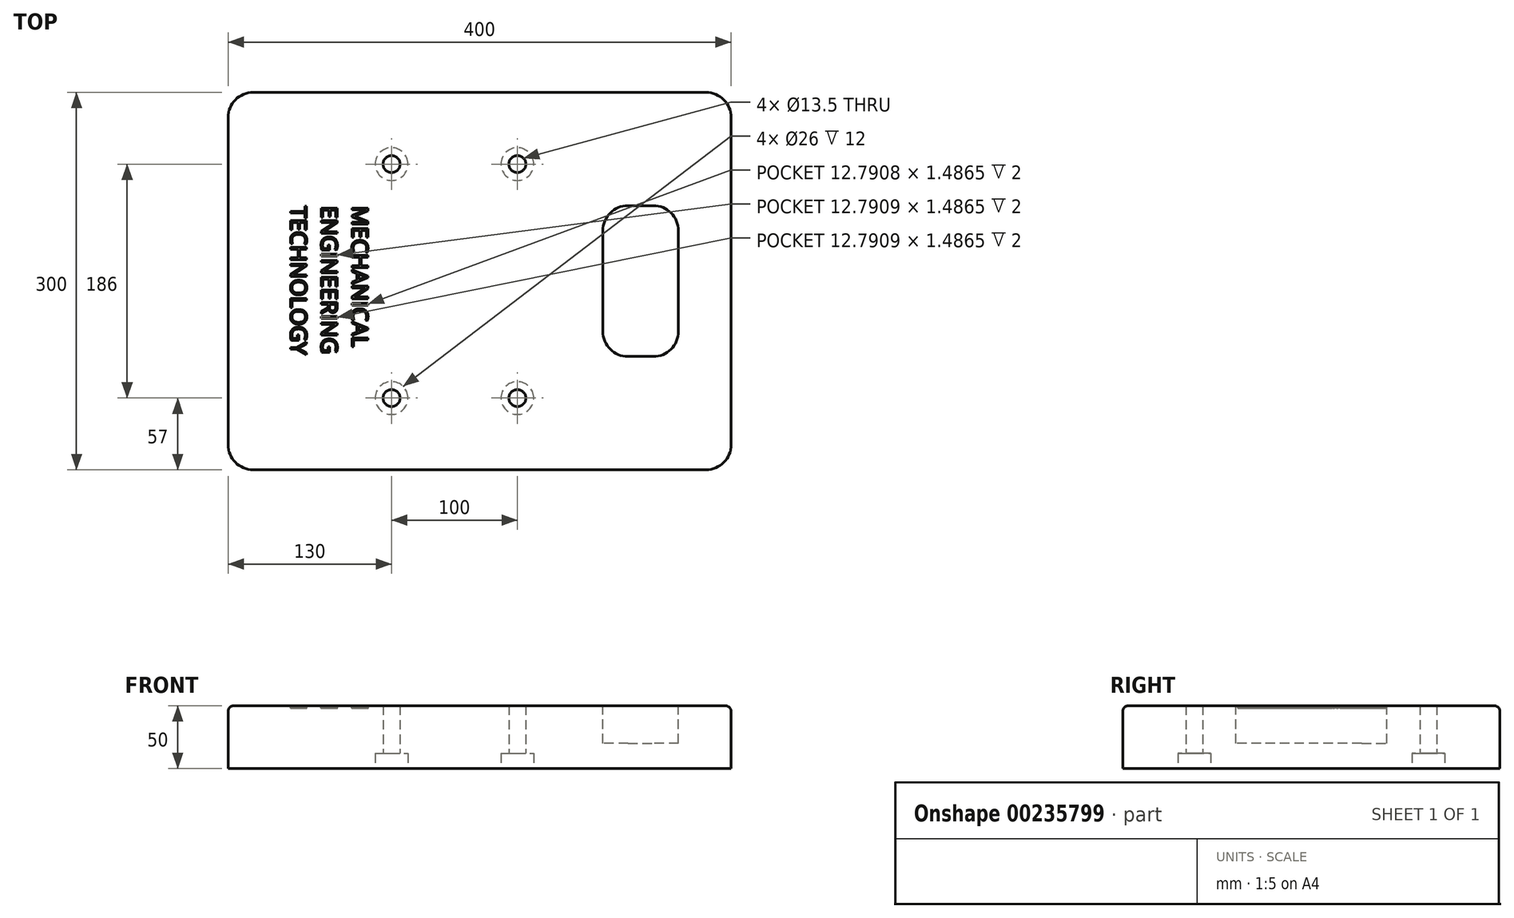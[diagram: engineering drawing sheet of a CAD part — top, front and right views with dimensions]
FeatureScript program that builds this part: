
annotation { "Feature Type Name" : "Feature", "Feature Type Description" : "" }
export const myFeature = defineFeature(function(context is Context, id is Id, definition is map)
    precondition{}
    {
        {
            var Q0;
            Q0=qCreatedBy(makeId("Top.planeOp"),FACE);
            var sketch = newSketch(context, id + "F0", { "sketchPlane" : qUnion([Q0])});
            skLineSegment(sketch, "E0", {"start": v(0, 0) * mm, "end": v(-200, 0) * mm});
            skLineSegment(sketch, "E1", {"start": v(-200, 0) * mm, "end": v(200, 0) * mm});
            skLineSegment(sketch, "E2", {"start": v(200, 0) * mm, "end": v(200, 150) * mm});
            skLineSegment(sketch, "E3", {"start": v(200, 150) * mm, "end": v(200, -150) * mm});
            skLineSegment(sketch, "E4", {"start": v(200, -150) * mm, "end": v(-200, -150) * mm});
            skLineSegment(sketch, "E5", {"start": v(-200, -150) * mm, "end": v(-200, 0) * mm});
            skLineSegment(sketch, "E6", {"start": v(-200, 0) * mm, "end": v(-200, 150) * mm});
            skLineSegment(sketch, "E7", {"start": v(-200, 150) * mm, "end": v(200, 150) * mm});
            skSolve(sketch);
        }
        {
            var Q0;
            {var subQ0=sQuery(id+"F0.wireOp",EDGE,"E4");Q0=makeQuery(id+"F0.imprint","IMPRINT",FACE,{"disambiguationData":[TD([[makeQuery(id+"F0.imprint","IMPRINT",EDGE,{"derivedFrom":subQ0}),-1.0]])]});}
            var Q1;
            {var subQ4=sQuery(id+"F0.wireOp",EDGE,"E6");Q1=makeQuery(id+"F0.imprint","IMPRINT",FACE,{"disambiguationData":[TD([[makeQuery(id+"F0.imprint","IMPRINT",EDGE,{"derivedFrom":subQ4}),-1.0]])]});}
            extrude(context, id + "F1", {"entities" : qUnion([Q0, Q1]), "depth" : 50 * mm});
        }
        {
            var Q0;
            Q0=makeQuery(id+"F1.opExtrude","SWEPT_EDGE",EDGE,{"disambiguationData":[OSD([sQuery(id+"F0.wireOp",EDGE,"E3"),sQuery(id+"F0.wireOp",EDGE,"E4")])]});
            var Q1;
            Q1=makeQuery(id+"F1.opExtrude","SWEPT_EDGE",EDGE,{"disambiguationData":[OSD([sQuery(id+"F0.wireOp",EDGE,"E3"),sQuery(id+"F0.wireOp",EDGE,"E7")])]});
            var Q2;
            Q2=makeQuery(id+"F1.opExtrude","SWEPT_EDGE",EDGE,{"disambiguationData":[OSD([sQuery(id+"F0.wireOp",EDGE,"E6"),sQuery(id+"F0.wireOp",EDGE,"E7")])]});
            var Q3;
            Q3=makeQuery(id+"F1.opExtrude","SWEPT_EDGE",EDGE,{"disambiguationData":[OSD([sQuery(id+"F0.wireOp",EDGE,"E4"),sQuery(id+"F0.wireOp",EDGE,"E5")])]});
            fillet(context, id + "F2", {"entities" : qUnion([Q0, Q1, Q2, Q3]), "radius" : 20 * mm, "tangentPropagation" : true, "allowEdgeOverflow" : false});
        }
        {
            var Q0;
            Q0=makeQuery(id+"F1.opExtrude","CAP_FACE",FACE,{"disambiguationData":[OSD([sQuery(id+"F0.wireOp",EDGE,"E3"),sQuery(id+"F0.wireOp",EDGE,"E4"),sQuery(id+"F0.wireOp",EDGE,"E5"),sQuery(id+"F0.wireOp",EDGE,"E6"),sQuery(id+"F0.wireOp",EDGE,"E7")])],"isStart":false});
            var sketch = newSketch(context, id + "F3", { "sketchPlane" : qUnion([Q0])});
            skLineSegment(sketch, "E8", {"start": v(-200, 0) * mm, "end": v(98, 0) * mm});
            skPoint(sketch, "E8.endSnap0", {"position": v(-200, 0) * mm});
            skLineSegment(sketch, "E9", {"start": v(98, 0) * mm, "end": v(98, 40) * mm});
            skLineSegment(sketch, "E10", {"start": v(118, 60) * mm, "end": v(138, 60) * mm});
            skLineSegment(sketch, "E11", {"start": v(158, 40) * mm, "end": v(158, -40) * mm});
            skLineSegment(sketch, "E12", {"start": v(138, -60) * mm, "end": v(118, -60) * mm});
            skLineSegment(sketch, "E13", {"start": v(98, -40) * mm, "end": v(98, 0) * mm});
            skPoint(sketch, "E14.visualSharp", {"position": v(158, -60) * mm});
            skArc(sketch, "E14.filletArc", {"start": v(138, -60) * mm, "mid": v(152.14, -54.14) * mm, "end": v(158, -40) * mm});
            skPoint(sketch, "E15.visualSharp", {"position": v(158, 60) * mm});
            skArc(sketch, "E15.filletArc", {"start": v(158, 40) * mm, "mid": v(152.14, 54.14) * mm, "end": v(138, 60) * mm});
            skPoint(sketch, "E16.visualSharp", {"position": v(98, 60) * mm});
            skArc(sketch, "E16.filletArc", {"start": v(118, 60) * mm, "mid": v(103.86, 54.14) * mm, "end": v(98, 40) * mm});
            skPoint(sketch, "E17.visualSharp", {"position": v(98, -60) * mm});
            skArc(sketch, "E17.filletArc", {"start": v(98, -40) * mm, "mid": v(103.86, -54.14) * mm, "end": v(118, -60) * mm});
            skSolve(sketch);
        }
        {
            var Q0;
            Q0=makeQuery(id+"F3.imprint","IMPRINT",FACE,{"disambiguationData":[TD([[makeQuery(id+"F3.imprint","IMPRINT",EDGE,{"derivedFrom":sQuery(id+"F3.wireOp",EDGE,"E9")}),-1.0]])]});
            extrude(context, id + "F4", {"entities" : qUnion([Q0]), "operationType" : NewBodyOperationType.REMOVE, "oppositeDirection" : true, "depth" : 30 * mm});
        }
        {
            var Q0;
            Q0=makeQuery(id+"F1.opExtrude","CAP_FACE",FACE,{"disambiguationData":[OSD([sQuery(id+"F0.wireOp",EDGE,"E3"),sQuery(id+"F0.wireOp",EDGE,"E4"),sQuery(id+"F0.wireOp",EDGE,"E5"),sQuery(id+"F0.wireOp",EDGE,"E6"),sQuery(id+"F0.wireOp",EDGE,"E7")])],"isStart":true});
            var sketch = newSketch(context, id + "F5", { "sketchPlane" : qUnion([Q0])});
            skLineSegment(sketch, "E18", {"start": v(200, -93) * mm, "end": v(30, -93) * mm});
            skLineSegment(sketch, "E19", {"start": v(30, -93) * mm, "end": v(30, 93) * mm});
            skLineSegment(sketch, "E20", {"start": v(30, 93) * mm, "end": v(-70, 93) * mm});
            skLineSegment(sketch, "E21", {"start": v(-70, 93) * mm, "end": v(-70, -93) * mm});
            skLineSegment(sketch, "E22", {"start": v(-70, -93) * mm, "end": v(30, -93) * mm});
            skCircle(sketch, "E23", {"center": v(30, 93) * mm, "radius": 6.75 * mm});
            skLineSegment(sketch, "E24", {"start": v(-20, -93) * mm, "end": v(-20, 93) * mm});
            skLineSegment(sketch, "E25", {"start": v(-70, 0) * mm, "end": v(30, 0) * mm});
            skCircle(sketch, "E26.MirrorC", {"center": v(-70, 93) * mm, "radius": 6.75 * mm});
            skCircle(sketch, "E27.MirrorC", {"center": v(-70, -93) * mm, "radius": 6.75 * mm});
            skCircle(sketch, "E28.MirrorC", {"center": v(30, -93) * mm, "radius": 6.75 * mm});
            skLineSegment(sketch, "E29", {"start": v(200, 0) * mm, "end": v(36.1, 0) * mm});
            skLineSegment(sketch, "E30", {"start": v(174.34, -93) * mm, "end": v(174.34, 0) * mm});
            skPoint(sketch, "E30.endSnap0", {"position": v(118.05, 0) * mm});
            skSolve(sketch);
        }
        {
            var Q0;
            Q0=sQuery(id+"F5.wireOp",VERTEX,"E21.start");
            var Q1;
            Q1=sQuery(id+"F5.wireOp",VERTEX,"E20.start");
            var Q2;
            Q2=sQuery(id+"F5.wireOp",VERTEX,"E22.end");
            var Q3;
            Q3=sQuery(id+"F5.wireOp",VERTEX,"E22.start");
            var Q4;
            Q4=makeQuery(id+"F1.opExtrude","SWEPT_BODY",BODY,{"disambiguationData":[OSD([sQuery(id+"F0.wireOp",EDGE,"E3"),sQuery(id+"F0.wireOp",EDGE,"E4"),sQuery(id+"F0.wireOp",EDGE,"E5"),sQuery(id+"F0.wireOp",EDGE,"E6"),sQuery(id+"F0.wireOp",EDGE,"E7")])]});
            hole(context, id + "F6", {"style" : HoleStyle.C_BORE, "endStyle" : HoleEndStyle.THROUGH, "holeDiameter" : 13.5 * mm, "cBoreDiameter" : 26 * mm, "cBoreDepth" : 12 * mm, "isTappedThrough" : true, "tappedDepth" : 20 * mm, "tapClearance" : 6, "locations" : qUnion([Q0, Q1, Q2, Q3]), "scope" : qUnion([Q4])});
        }
        {
            var Q0;
            Q0=makeQuery(id+"F1.opExtrude","CAP_FACE",FACE,{"disambiguationData":[OSD([sQuery(id+"F0.wireOp",EDGE,"E3"),sQuery(id+"F0.wireOp",EDGE,"E4"),sQuery(id+"F0.wireOp",EDGE,"E5"),sQuery(id+"F0.wireOp",EDGE,"E6"),sQuery(id+"F0.wireOp",EDGE,"E7")])],"isStart":false});
            var sketch = newSketch(context, id + "F7", { "sketchPlane" : qUnion([Q0])});
            skPoint(sketch, "E31.secondSnap0", {"position": v(-194.14, -144.14) * mm});
            skPoint(sketch, "E32.endSnap0", {"position": v(-200, 0) * mm});
            skText(sketch, "E33", { "text": "MECHANICAL\nENGINEERING \nTECHNOLOGY", "fontName": "OpenSans-Regular.ttf"});
            const initialGuessF7  = {"E33": [-0.10155, 0.05969, 0, -1, 0.0129]};
            skSetInitialGuess(sketch, initialGuessF7);
            skSolve(sketch);
        }
        {
            var Q0;
            Q0 = qSketchRegion(id + "F7", true);
            extrude(context, id + "F8", {"entities" : qUnion([Q0]), "operationType" : NewBodyOperationType.REMOVE, "oppositeDirection" : true, "depth" : 2 * mm});
        }
        {
            var Q0;
            Q0=makeQuery(id+"F1.opExtrude","CAP_EDGE",EDGE,{"disambiguationData":[OSD([sQuery(id+"F0.wireOp",EDGE,"E5"),sQuery(id+"F0.wireOp",EDGE,"E6")])],"isStart":false});
            fillet(context, id + "F9", {"entities" : qUnion([Q0]), "radius" : 5 * mm, "tangentPropagation" : true, "allowEdgeOverflow" : false});
        }
    });
